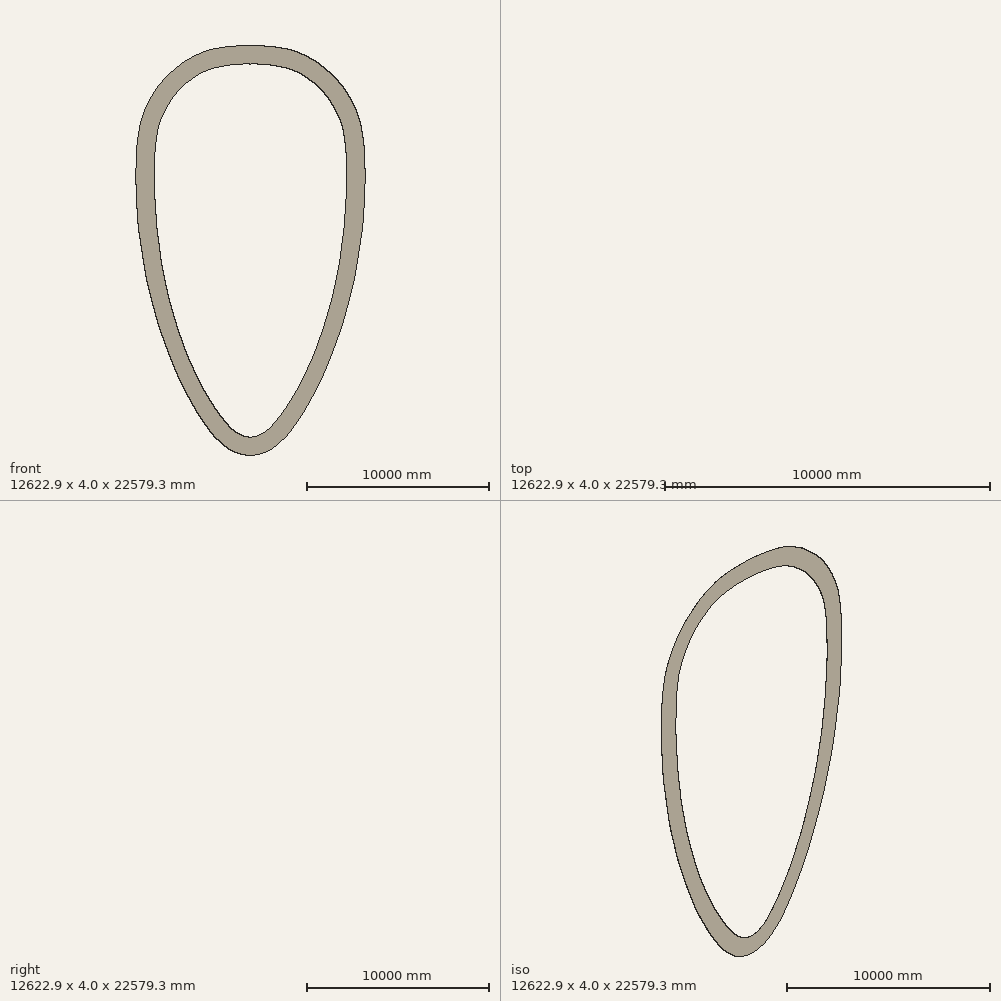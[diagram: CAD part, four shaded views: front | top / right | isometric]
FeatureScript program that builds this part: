
annotation { "Feature Type Name" : "Feature", "Feature Type Description" : "" }
export const myFeature = defineFeature(function(context is Context, id is Id, definition is map)
    precondition{}
    {
        {
            var Q0;
            Q0=qCreatedBy(makeId("Front.planeOp"),FACE);
            var sketch = newSketch(context, id + "F0", { "sketchPlane" : qUnion([Q0])});
            skLineSegment(sketch, "E0", {"start": v(0, -11289.64) * mm, "end": v(-7.01, -11162.82) * mm});
            skLineSegment(sketch, "E1", {"start": v(-7.01, -11162.82) * mm, "end": v(0, -11289.64) * mm});
            skLineSegment(sketch, "E2", {"start": v(0, -11289.64) * mm, "end": v(-111.94, -11283.44) * mm});
            skLineSegment(sketch, "E3", {"start": v(-111.94, -11283.44) * mm, "end": v(-223.42, -11271.8) * mm});
            skLineSegment(sketch, "E4", {"start": v(-223.42, -11271.8) * mm, "end": v(-504.04, -11216.64) * mm});
            skLineSegment(sketch, "E5", {"start": v(-504.04, -11216.64) * mm, "end": v(-777.95, -11130.79) * mm});
            skLineSegment(sketch, "E6", {"start": v(-777.95, -11130.79) * mm, "end": v(-980.67, -11048.11) * mm});
            skLineSegment(sketch, "E7", {"start": v(-980.67, -11048.11) * mm, "end": v(-1172.64, -10945.8) * mm});
            skLineSegment(sketch, "E8", {"start": v(-1172.64, -10945.8) * mm, "end": v(-1407.5, -10773.28) * mm});
            skLineSegment(sketch, "E9", {"start": v(-1407.5, -10773.28) * mm, "end": v(-1628.17, -10579.5) * mm});
            skLineSegment(sketch, "E10", {"start": v(-1628.17, -10579.5) * mm, "end": v(-1825.42, -10402.14) * mm});
            skLineSegment(sketch, "E11", {"start": v(-1825.42, -10402.14) * mm, "end": v(-2012.87, -10216.57) * mm});
            skLineSegment(sketch, "E12", {"start": v(-2012.87, -10216.57) * mm, "end": v(-2227.38, -9954.46) * mm});
            skLineSegment(sketch, "E13", {"start": v(-2227.38, -9954.46) * mm, "end": v(-2424.63, -9676.9) * mm});
            skLineSegment(sketch, "E14", {"start": v(-2424.63, -9676.9) * mm, "end": v(-2700.9, -9278.24) * mm});
            skLineSegment(sketch, "E15", {"start": v(-2700.9, -9278.24) * mm, "end": v(-2963.4, -8872.04) * mm});
            skLineSegment(sketch, "E16", {"start": v(-2963.4, -8872.04) * mm, "end": v(-3166.72, -8516.54) * mm});
            skLineSegment(sketch, "E17", {"start": v(-3166.72, -8516.54) * mm, "end": v(-3362.58, -8156.37) * mm});
            skLineSegment(sketch, "E18", {"start": v(-3362.58, -8156.37) * mm, "end": v(-3412.39, -8065.52) * mm});
            skLineSegment(sketch, "E19", {"start": v(-3412.39, -8065.52) * mm, "end": v(-3575.86, -7775.73) * mm});
            skLineSegment(sketch, "E20", {"start": v(-3575.86, -7775.73) * mm, "end": v(-3757.6, -7429.63) * mm});
            skLineSegment(sketch, "E21", {"start": v(-3757.6, -7429.63) * mm, "end": v(-3926.43, -7077.15) * mm});
            skLineSegment(sketch, "E22", {"start": v(-3926.43, -7077.15) * mm, "end": v(-4036.82, -6824.98) * mm});
            skLineSegment(sketch, "E23", {"start": v(-4036.82, -6824.98) * mm, "end": v(-4141.67, -6570.42) * mm});
            skLineSegment(sketch, "E24", {"start": v(-4141.67, -6570.42) * mm, "end": v(-4331.8, -6091.94) * mm});
            skLineSegment(sketch, "E25", {"start": v(-4331.8, -6091.94) * mm, "end": v(-4436, -5835.24) * mm});
            skLineSegment(sketch, "E26", {"start": v(-4436, -5835.24) * mm, "end": v(-4538.65, -5577.94) * mm});
            skLineSegment(sketch, "E27", {"start": v(-4538.65, -5577.94) * mm, "end": v(-4659.73, -5254.02) * mm});
            skLineSegment(sketch, "E28", {"start": v(-4659.73, -5254.02) * mm, "end": v(-4776.7, -4928.49) * mm});
            skLineSegment(sketch, "E29", {"start": v(-4776.7, -4928.49) * mm, "end": v(-4898.87, -4588.51) * mm});
            skLineSegment(sketch, "E30", {"start": v(-4898.87, -4588.51) * mm, "end": v(-5017.16, -4247.21) * mm});
            skLineSegment(sketch, "E31", {"start": v(-5017.16, -4247.21) * mm, "end": v(-5124.27, -3909.8) * mm});
            skLineSegment(sketch, "E32", {"start": v(-5124.27, -3909.8) * mm, "end": v(-5221.15, -3569.3) * mm});
            skLineSegment(sketch, "E33", {"start": v(-5221.15, -3569.3) * mm, "end": v(-5238.27, -3504.46) * mm});
            skLineSegment(sketch, "E34", {"start": v(-5238.27, -3504.46) * mm, "end": v(-5325.82, -3176.37) * mm});
            skLineSegment(sketch, "E35", {"start": v(-5325.82, -3176.37) * mm, "end": v(-5411.01, -2847.6) * mm});
            skLineSegment(sketch, "E36", {"start": v(-5411.01, -2847.6) * mm, "end": v(-5529.91, -2400.35) * mm});
            skLineSegment(sketch, "E37", {"start": v(-5529.91, -2400.35) * mm, "end": v(-5642.94, -1951.71) * mm});
            skLineSegment(sketch, "E38", {"start": v(-5642.94, -1951.71) * mm, "end": v(-5743.55, -1477.9) * mm});
            skLineSegment(sketch, "E39", {"start": v(-5743.55, -1477.9) * mm, "end": v(-5829.55, -1001.01) * mm});
            skLineSegment(sketch, "E40", {"start": v(-5829.55, -1001.01) * mm, "end": v(-5936.31, -331.14) * mm});
            skLineSegment(sketch, "E41", {"start": v(-5936.31, -331.14) * mm, "end": v(-5988.84, 26.4) * mm});
            skLineSegment(sketch, "E42", {"start": v(-5988.84, 26.4) * mm, "end": v(-6043.32, 383.62) * mm});
            skLineSegment(sketch, "E43", {"start": v(-6043.32, 383.62) * mm, "end": v(-6096.81, 707.31) * mm});
            skLineSegment(sketch, "E44", {"start": v(-6096.81, 707.31) * mm, "end": v(-6146.65, 1031.52) * mm});
            skLineSegment(sketch, "E45", {"start": v(-6146.65, 1031.52) * mm, "end": v(-6183.68, 1335.68) * mm});
            skLineSegment(sketch, "E46", {"start": v(-6183.68, 1335.68) * mm, "end": v(-6057.6, 1351.03) * mm});
            skLineSegment(sketch, "E47", {"start": v(-6057.6, 1351.03) * mm, "end": v(-6183.68, 1335.68) * mm});
            skLineSegment(sketch, "E48", {"start": v(-6183.68, 1335.68) * mm, "end": v(-6226.6, 1881.8) * mm});
            skLineSegment(sketch, "E49", {"start": v(-6226.6, 1881.8) * mm, "end": v(-6258.26, 2428.67) * mm});
            skLineSegment(sketch, "E50", {"start": v(-6258.26, 2428.67) * mm, "end": v(-6272.23, 2791.2) * mm});
            skLineSegment(sketch, "E51", {"start": v(-6272.23, 2791.2) * mm, "end": v(-6285.94, 3153.77) * mm});
            skLineSegment(sketch, "E52", {"start": v(-6285.94, 3153.77) * mm, "end": v(-6300.55, 3466.54) * mm});
            skLineSegment(sketch, "E53", {"start": v(-6300.55, 3466.54) * mm, "end": v(-6311.37, 3779.4) * mm});
            skLineSegment(sketch, "E54", {"start": v(-6311.37, 3779.4) * mm, "end": v(-6311.47, 4250.1) * mm});
            skLineSegment(sketch, "E55", {"start": v(-6311.47, 4250.1) * mm, "end": v(-6310.8, 4321.48) * mm});
            skLineSegment(sketch, "E56", {"start": v(-6310.8, 4321.48) * mm, "end": v(-6183.8, 4320.29) * mm});
            skLineSegment(sketch, "E57", {"start": v(-6183.8, 4320.29) * mm, "end": v(-6310.8, 4321.48) * mm});
            skLineSegment(sketch, "E58", {"start": v(-6310.8, 4321.48) * mm, "end": v(-6297.68, 4798.67) * mm});
            skLineSegment(sketch, "E59", {"start": v(-6297.68, 4798.67) * mm, "end": v(-6272.6, 5435.52) * mm});
            skLineSegment(sketch, "E60", {"start": v(-6272.6, 5435.52) * mm, "end": v(-6258.69, 5683.58) * mm});
            skLineSegment(sketch, "E61", {"start": v(-6258.69, 5683.58) * mm, "end": v(-6237.5, 5930.98) * mm});
            skLineSegment(sketch, "E62", {"start": v(-6237.5, 5930.98) * mm, "end": v(-6203.85, 6188.94) * mm});
            skLineSegment(sketch, "E63", {"start": v(-6203.85, 6188.94) * mm, "end": v(-6162.65, 6445.94) * mm});
            skLineSegment(sketch, "E64", {"start": v(-6162.65, 6445.94) * mm, "end": v(-6110.12, 6747.69) * mm});
            skLineSegment(sketch, "E65", {"start": v(-6110.12, 6747.69) * mm, "end": v(-6051.35, 7048.2) * mm});
            skLineSegment(sketch, "E66", {"start": v(-6051.35, 7048.2) * mm, "end": v(-5926.7, 7023.81) * mm});
            skLineSegment(sketch, "E67", {"start": v(-5926.7, 7023.81) * mm, "end": v(-6051.35, 7048.2) * mm});
            skLineSegment(sketch, "E68", {"start": v(-6051.35, 7048.2) * mm, "end": v(-6042.96, 7077.02) * mm});
            skLineSegment(sketch, "E69", {"start": v(-6042.96, 7077.02) * mm, "end": v(-6029.68, 7122.08) * mm});
            skLineSegment(sketch, "E70", {"start": v(-6029.68, 7122.08) * mm, "end": v(-5926.38, 7441.9) * mm});
            skLineSegment(sketch, "E71", {"start": v(-5926.38, 7441.9) * mm, "end": v(-5868.31, 7599.55) * mm});
            skLineSegment(sketch, "E72", {"start": v(-5868.31, 7599.55) * mm, "end": v(-5805.22, 7755.18) * mm});
            skLineSegment(sketch, "E73", {"start": v(-5805.22, 7755.18) * mm, "end": v(-5655.36, 8075.96) * mm});
            skLineSegment(sketch, "E74", {"start": v(-5655.36, 8075.96) * mm, "end": v(-5489.37, 8389.29) * mm});
            skLineSegment(sketch, "E75", {"start": v(-5489.37, 8389.29) * mm, "end": v(-5349.98, 8633.54) * mm});
            skLineSegment(sketch, "E76", {"start": v(-5349.98, 8633.54) * mm, "end": v(-5197.63, 8869.15) * mm});
            skLineSegment(sketch, "E77", {"start": v(-5197.63, 8869.15) * mm, "end": v(-5044.92, 9070.62) * mm});
            skLineSegment(sketch, "E78", {"start": v(-5044.92, 9070.62) * mm, "end": v(-4884.22, 9266.38) * mm});
            skLineSegment(sketch, "E79", {"start": v(-4884.22, 9266.38) * mm, "end": v(-4774.2, 9397.95) * mm});
            skLineSegment(sketch, "E80", {"start": v(-4774.2, 9397.95) * mm, "end": v(-4659.93, 9525.56) * mm});
            skLineSegment(sketch, "E81", {"start": v(-4659.93, 9525.56) * mm, "end": v(-4549.3, 9635.08) * mm});
            skLineSegment(sketch, "E82", {"start": v(-4549.3, 9635.08) * mm, "end": v(-4432.96, 9738.61) * mm});
            skLineSegment(sketch, "E83", {"start": v(-4432.96, 9738.61) * mm, "end": v(-4348.53, 9643.74) * mm});
            skLineSegment(sketch, "E84", {"start": v(-4348.53, 9643.74) * mm, "end": v(-4432.96, 9738.61) * mm});
            skLineSegment(sketch, "E85", {"start": v(-4432.96, 9738.61) * mm, "end": v(-4092.55, 10032.06) * mm});
            skLineSegment(sketch, "E86", {"start": v(-4092.55, 10032.06) * mm, "end": v(-3818.92, 10253.22) * mm});
            skLineSegment(sketch, "E87", {"start": v(-3818.92, 10253.22) * mm, "end": v(-3693.57, 10351.47) * mm});
            skLineSegment(sketch, "E88", {"start": v(-3693.57, 10351.47) * mm, "end": v(-3563.44, 10442.37) * mm});
            skLineSegment(sketch, "E89", {"start": v(-3563.44, 10442.37) * mm, "end": v(-3397.07, 10536.07) * mm});
            skLineSegment(sketch, "E90", {"start": v(-3397.07, 10536.07) * mm, "end": v(-3226.64, 10623.58) * mm});
            skLineSegment(sketch, "E91", {"start": v(-3226.64, 10623.58) * mm, "end": v(-3085.77, 10700.23) * mm});
            skLineSegment(sketch, "E92", {"start": v(-3085.77, 10700.23) * mm, "end": v(-2943.68, 10773.84) * mm});
            skLineSegment(sketch, "E93", {"start": v(-2943.68, 10773.84) * mm, "end": v(-2811.25, 10832.34) * mm});
            skLineSegment(sketch, "E94", {"start": v(-2811.25, 10832.34) * mm, "end": v(-2677.62, 10888.8) * mm});
            skLineSegment(sketch, "E95", {"start": v(-2677.62, 10888.8) * mm, "end": v(-2562.5, 10940.26) * mm});
            skLineSegment(sketch, "E96", {"start": v(-2562.5, 10940.26) * mm, "end": v(-2446.17, 10987.91) * mm});
            skLineSegment(sketch, "E97", {"start": v(-2446.17, 10987.91) * mm, "end": v(-2293.52, 11034.06) * mm});
            skLineSegment(sketch, "E98", {"start": v(-2293.52, 11034.06) * mm, "end": v(-2137.44, 11070.06) * mm});
            skLineSegment(sketch, "E99", {"start": v(-2137.44, 11070.06) * mm, "end": v(-1844.04, 11131.85) * mm});
            skLineSegment(sketch, "E100", {"start": v(-1844.04, 11131.85) * mm, "end": v(-1549.48, 11183.54) * mm});
            skLineSegment(sketch, "E101", {"start": v(-1549.48, 11183.54) * mm, "end": v(-1246.78, 11220.3) * mm});
            skLineSegment(sketch, "E102", {"start": v(-1246.78, 11220.3) * mm, "end": v(-942.8, 11248.44) * mm});
            skLineSegment(sketch, "E103", {"start": v(-942.8, 11248.44) * mm, "end": v(-598.45, 11277) * mm});
            skLineSegment(sketch, "E104", {"start": v(-598.45, 11277) * mm, "end": v(-299.39, 11289.51) * mm});
            skLineSegment(sketch, "E105", {"start": v(-299.39, 11289.51) * mm, "end": v(0, 11289.64) * mm});
            skLineSegment(sketch, "E106", {"start": v(0, 11289.64) * mm, "end": v(0.05, 11162.64) * mm});
            skLineSegment(sketch, "E107", {"start": v(0.05, 11162.64) * mm, "end": v(0, 11289.64) * mm});
            skLineSegment(sketch, "E108", {"start": v(0, 11289.64) * mm, "end": v(299.36, 11289.51) * mm});
            skLineSegment(sketch, "E109", {"start": v(299.36, 11289.51) * mm, "end": v(598.42, 11277) * mm});
            skLineSegment(sketch, "E110", {"start": v(598.42, 11277) * mm, "end": v(942.8, 11248.44) * mm});
            skLineSegment(sketch, "E111", {"start": v(942.8, 11248.44) * mm, "end": v(1246.78, 11220.3) * mm});
            skLineSegment(sketch, "E112", {"start": v(1246.78, 11220.3) * mm, "end": v(1549.48, 11183.54) * mm});
            skLineSegment(sketch, "E113", {"start": v(1549.48, 11183.54) * mm, "end": v(1844.04, 11131.85) * mm});
            skLineSegment(sketch, "E114", {"start": v(1844.04, 11131.85) * mm, "end": v(2137.44, 11070.06) * mm});
            skLineSegment(sketch, "E115", {"start": v(2137.44, 11070.06) * mm, "end": v(2293.5, 11034.06) * mm});
            skLineSegment(sketch, "E116", {"start": v(2293.5, 11034.06) * mm, "end": v(2446.15, 10987.91) * mm});
            skLineSegment(sketch, "E117", {"start": v(2446.15, 10987.91) * mm, "end": v(2562.5, 10940.26) * mm});
            skLineSegment(sketch, "E118", {"start": v(2562.5, 10940.26) * mm, "end": v(2677.6, 10888.8) * mm});
            skLineSegment(sketch, "E119", {"start": v(2677.6, 10888.8) * mm, "end": v(2811.25, 10832.34) * mm});
            skLineSegment(sketch, "E120", {"start": v(2811.25, 10832.34) * mm, "end": v(2943.68, 10773.84) * mm});
            skLineSegment(sketch, "E121", {"start": v(2943.68, 10773.84) * mm, "end": v(3085.74, 10700.23) * mm});
            skLineSegment(sketch, "E122", {"start": v(3085.74, 10700.23) * mm, "end": v(3226.61, 10623.58) * mm});
            skLineSegment(sketch, "E123", {"start": v(3226.61, 10623.58) * mm, "end": v(3397.07, 10536.07) * mm});
            skLineSegment(sketch, "E124", {"start": v(3397.07, 10536.07) * mm, "end": v(3563.44, 10442.37) * mm});
            skLineSegment(sketch, "E125", {"start": v(3563.44, 10442.37) * mm, "end": v(3693.57, 10351.47) * mm});
            skLineSegment(sketch, "E126", {"start": v(3693.57, 10351.47) * mm, "end": v(3818.9, 10253.22) * mm});
            skLineSegment(sketch, "E127", {"start": v(3818.9, 10253.22) * mm, "end": v(4092.55, 10032.06) * mm});
            skLineSegment(sketch, "E128", {"start": v(4092.55, 10032.06) * mm, "end": v(4432.96, 9738.61) * mm});
            skLineSegment(sketch, "E129", {"start": v(4432.96, 9738.61) * mm, "end": v(4350.03, 9642.42) * mm});
            skLineSegment(sketch, "E130", {"start": v(4350.03, 9642.42) * mm, "end": v(4432.96, 9738.61) * mm});
            skLineSegment(sketch, "E131", {"start": v(4432.96, 9738.61) * mm, "end": v(4549.3, 9635.08) * mm});
            skLineSegment(sketch, "E132", {"start": v(4549.3, 9635.08) * mm, "end": v(4659.93, 9525.56) * mm});
            skLineSegment(sketch, "E133", {"start": v(4659.93, 9525.56) * mm, "end": v(4774.2, 9397.95) * mm});
            skLineSegment(sketch, "E134", {"start": v(4774.2, 9397.95) * mm, "end": v(4884.22, 9266.38) * mm});
            skLineSegment(sketch, "E135", {"start": v(4884.22, 9266.38) * mm, "end": v(5044.92, 9070.62) * mm});
            skLineSegment(sketch, "E136", {"start": v(5044.92, 9070.62) * mm, "end": v(5197.6, 8869.15) * mm});
            skLineSegment(sketch, "E137", {"start": v(5197.6, 8869.15) * mm, "end": v(5349.95, 8633.54) * mm});
            skLineSegment(sketch, "E138", {"start": v(5349.95, 8633.54) * mm, "end": v(5489.35, 8389.29) * mm});
            skLineSegment(sketch, "E139", {"start": v(5489.35, 8389.29) * mm, "end": v(5655.36, 8075.96) * mm});
            skLineSegment(sketch, "E140", {"start": v(5655.36, 8075.96) * mm, "end": v(5805.2, 7755.18) * mm});
            skLineSegment(sketch, "E141", {"start": v(5805.2, 7755.18) * mm, "end": v(5868.31, 7599.55) * mm});
            skLineSegment(sketch, "E142", {"start": v(5868.31, 7599.55) * mm, "end": v(5926.38, 7441.9) * mm});
            skLineSegment(sketch, "E143", {"start": v(5926.38, 7441.9) * mm, "end": v(6029.68, 7122.08) * mm});
            skLineSegment(sketch, "E144", {"start": v(6029.68, 7122.08) * mm, "end": v(6042.96, 7077.02) * mm});
            skLineSegment(sketch, "E145", {"start": v(6042.96, 7077.02) * mm, "end": v(6051.32, 7048.2) * mm});
            skLineSegment(sketch, "E146", {"start": v(6051.32, 7048.2) * mm, "end": v(5929.38, 7012.79) * mm});
            skLineSegment(sketch, "E147", {"start": v(5929.38, 7012.79) * mm, "end": v(6051.32, 7048.2) * mm});
            skLineSegment(sketch, "E148", {"start": v(6051.32, 7048.2) * mm, "end": v(6110.12, 6747.69) * mm});
            skLineSegment(sketch, "E149", {"start": v(6110.12, 6747.69) * mm, "end": v(6162.62, 6445.94) * mm});
            skLineSegment(sketch, "E150", {"start": v(6162.62, 6445.94) * mm, "end": v(6203.85, 6188.94) * mm});
            skLineSegment(sketch, "E151", {"start": v(6203.85, 6188.94) * mm, "end": v(6237.48, 5930.98) * mm});
            skLineSegment(sketch, "E152", {"start": v(6237.48, 5930.98) * mm, "end": v(6258.69, 5683.58) * mm});
            skLineSegment(sketch, "E153", {"start": v(6258.69, 5683.58) * mm, "end": v(6272.6, 5435.52) * mm});
            skLineSegment(sketch, "E154", {"start": v(6272.6, 5435.52) * mm, "end": v(6297.68, 4798.67) * mm});
            skLineSegment(sketch, "E155", {"start": v(6297.68, 4798.67) * mm, "end": v(6310.78, 4321.48) * mm});
            skLineSegment(sketch, "E156", {"start": v(6310.78, 4321.48) * mm, "end": v(6183.83, 4317.97) * mm});
            skLineSegment(sketch, "E157", {"start": v(6183.83, 4317.97) * mm, "end": v(6310.78, 4321.48) * mm});
            skLineSegment(sketch, "E158", {"start": v(6310.78, 4321.48) * mm, "end": v(6311.47, 4250.1) * mm});
            skLineSegment(sketch, "E159", {"start": v(6311.47, 4250.1) * mm, "end": v(6311.37, 3779.4) * mm});
            skLineSegment(sketch, "E160", {"start": v(6311.37, 3779.4) * mm, "end": v(6300.52, 3466.54) * mm});
            skLineSegment(sketch, "E161", {"start": v(6300.52, 3466.54) * mm, "end": v(6285.94, 3153.77) * mm});
            skLineSegment(sketch, "E162", {"start": v(6285.94, 3153.77) * mm, "end": v(6272.2, 2791.2) * mm});
            skLineSegment(sketch, "E163", {"start": v(6272.2, 2791.2) * mm, "end": v(6258.26, 2428.67) * mm});
            skLineSegment(sketch, "E164", {"start": v(6258.26, 2428.67) * mm, "end": v(6226.58, 1881.8) * mm});
            skLineSegment(sketch, "E165", {"start": v(6226.58, 1881.8) * mm, "end": v(6183.68, 1335.68) * mm});
            skLineSegment(sketch, "E166", {"start": v(6183.68, 1335.68) * mm, "end": v(6057.06, 1345.64) * mm});
            skLineSegment(sketch, "E167", {"start": v(6057.06, 1345.64) * mm, "end": v(6183.68, 1335.68) * mm});
            skLineSegment(sketch, "E168", {"start": v(6183.68, 1335.68) * mm, "end": v(6146.65, 1031.52) * mm});
            skLineSegment(sketch, "E169", {"start": v(6146.65, 1031.52) * mm, "end": v(6096.79, 707.31) * mm});
            skLineSegment(sketch, "E170", {"start": v(6096.79, 707.31) * mm, "end": v(6043.32, 383.62) * mm});
            skLineSegment(sketch, "E171", {"start": v(6043.32, 383.62) * mm, "end": v(5988.81, 26.4) * mm});
            skLineSegment(sketch, "E172", {"start": v(5988.81, 26.4) * mm, "end": v(5936.31, -331.14) * mm});
            skLineSegment(sketch, "E173", {"start": v(5936.31, -331.14) * mm, "end": v(5829.55, -1001.01) * mm});
            skLineSegment(sketch, "E174", {"start": v(5829.55, -1001.01) * mm, "end": v(5743.55, -1477.9) * mm});
            skLineSegment(sketch, "E175", {"start": v(5743.55, -1477.9) * mm, "end": v(5642.94, -1951.71) * mm});
            skLineSegment(sketch, "E176", {"start": v(5642.94, -1951.71) * mm, "end": v(5529.91, -2400.35) * mm});
            skLineSegment(sketch, "E177", {"start": v(5529.91, -2400.35) * mm, "end": v(5410.99, -2847.6) * mm});
            skLineSegment(sketch, "E178", {"start": v(5410.99, -2847.6) * mm, "end": v(5325.82, -3176.37) * mm});
            skLineSegment(sketch, "E179", {"start": v(5325.82, -3176.37) * mm, "end": v(5238.27, -3504.46) * mm});
            skLineSegment(sketch, "E180", {"start": v(5238.27, -3504.46) * mm, "end": v(5221.12, -3569.3) * mm});
            skLineSegment(sketch, "E181", {"start": v(5221.12, -3569.3) * mm, "end": v(5124.27, -3909.8) * mm});
            skLineSegment(sketch, "E182", {"start": v(5124.27, -3909.8) * mm, "end": v(5017.14, -4247.21) * mm});
            skLineSegment(sketch, "E183", {"start": v(5017.14, -4247.21) * mm, "end": v(4898.87, -4588.51) * mm});
            skLineSegment(sketch, "E184", {"start": v(4898.87, -4588.51) * mm, "end": v(4776.7, -4928.49) * mm});
            skLineSegment(sketch, "E185", {"start": v(4776.7, -4928.49) * mm, "end": v(4659.73, -5254.02) * mm});
            skLineSegment(sketch, "E186", {"start": v(4659.73, -5254.02) * mm, "end": v(4538.65, -5577.94) * mm});
            skLineSegment(sketch, "E187", {"start": v(4538.65, -5577.94) * mm, "end": v(4435.98, -5835.24) * mm});
            skLineSegment(sketch, "E188", {"start": v(4435.98, -5835.24) * mm, "end": v(4331.8, -6091.94) * mm});
            skLineSegment(sketch, "E189", {"start": v(4331.8, -6091.94) * mm, "end": v(4141.67, -6570.42) * mm});
            skLineSegment(sketch, "E190", {"start": v(4141.67, -6570.42) * mm, "end": v(4036.82, -6824.98) * mm});
            skLineSegment(sketch, "E191", {"start": v(4036.82, -6824.98) * mm, "end": v(3926.43, -7077.15) * mm});
            skLineSegment(sketch, "E192", {"start": v(3926.43, -7077.15) * mm, "end": v(3757.57, -7429.63) * mm});
            skLineSegment(sketch, "E193", {"start": v(3757.57, -7429.63) * mm, "end": v(3575.86, -7775.73) * mm});
            skLineSegment(sketch, "E194", {"start": v(3575.86, -7775.73) * mm, "end": v(3412.39, -8065.52) * mm});
            skLineSegment(sketch, "E195", {"start": v(3412.39, -8065.52) * mm, "end": v(3362.58, -8156.37) * mm});
            skLineSegment(sketch, "E196", {"start": v(3362.58, -8156.37) * mm, "end": v(3166.72, -8516.54) * mm});
            skLineSegment(sketch, "E197", {"start": v(3166.72, -8516.54) * mm, "end": v(2963.37, -8872.04) * mm});
            skLineSegment(sketch, "E198", {"start": v(2963.37, -8872.04) * mm, "end": v(2700.9, -9278.24) * mm});
            skLineSegment(sketch, "E199", {"start": v(2700.9, -9278.24) * mm, "end": v(2424.63, -9676.9) * mm});
            skLineSegment(sketch, "E200", {"start": v(2424.63, -9676.9) * mm, "end": v(2227.38, -9954.46) * mm});
            skLineSegment(sketch, "E201", {"start": v(2227.38, -9954.46) * mm, "end": v(2012.87, -10216.57) * mm});
            skLineSegment(sketch, "E202", {"start": v(2012.87, -10216.57) * mm, "end": v(1825.42, -10402.14) * mm});
            skLineSegment(sketch, "E203", {"start": v(1825.42, -10402.14) * mm, "end": v(1628.17, -10579.5) * mm});
            skLineSegment(sketch, "E204", {"start": v(1628.17, -10579.5) * mm, "end": v(1407.5, -10773.28) * mm});
            skLineSegment(sketch, "E205", {"start": v(1407.5, -10773.28) * mm, "end": v(1172.64, -10945.8) * mm});
            skLineSegment(sketch, "E206", {"start": v(1172.64, -10945.8) * mm, "end": v(980.64, -11048.11) * mm});
            skLineSegment(sketch, "E207", {"start": v(980.64, -11048.11) * mm, "end": v(777.95, -11130.79) * mm});
            skLineSegment(sketch, "E208", {"start": v(777.95, -11130.79) * mm, "end": v(504.01, -11216.64) * mm});
            skLineSegment(sketch, "E209", {"start": v(504.01, -11216.64) * mm, "end": v(223.42, -11271.8) * mm});
            skLineSegment(sketch, "E210", {"start": v(223.42, -11271.8) * mm, "end": v(111.94, -11283.44) * mm});
            skLineSegment(sketch, "E211", {"start": v(111.94, -11283.44) * mm, "end": v(0, -11289.64) * mm});
            skLineSegment(sketch, "E212", {"start": v(0, 10265.23) * mm, "end": v(0, 10392.23) * mm});
            skLineSegment(sketch, "E213", {"start": v(0, 10392.23) * mm, "end": v(0, 10265.23) * mm});
            skLineSegment(sketch, "E214", {"start": v(0, 10265.23) * mm, "end": v(-81.61, 10275.32) * mm});
            skLineSegment(sketch, "E215", {"start": v(-81.61, 10275.32) * mm, "end": v(-163.65, 10280.1) * mm});
            skLineSegment(sketch, "E216", {"start": v(-163.65, 10280.1) * mm, "end": v(-273.76, 10277.25) * mm});
            skLineSegment(sketch, "E217", {"start": v(-273.76, 10277.25) * mm, "end": v(-383.84, 10269.32) * mm});
            skLineSegment(sketch, "E218", {"start": v(-383.84, 10269.32) * mm, "end": v(-668.8, 10252.76) * mm});
            skLineSegment(sketch, "E219", {"start": v(-668.8, 10252.76) * mm, "end": v(-953.1, 10232.64) * mm});
            skLineSegment(sketch, "E220", {"start": v(-953.1, 10232.64) * mm, "end": v(-1208.6, 10199.7) * mm});
            skLineSegment(sketch, "E221", {"start": v(-1208.6, 10199.7) * mm, "end": v(-1462.74, 10156.16) * mm});
            skLineSegment(sketch, "E222", {"start": v(-1462.74, 10156.16) * mm, "end": v(-1503.83, 10148.57) * mm});
            skLineSegment(sketch, "E223", {"start": v(-1503.83, 10148.57) * mm, "end": v(-1823.14, 10083.44) * mm});
            skLineSegment(sketch, "E224", {"start": v(-1823.14, 10083.44) * mm, "end": v(-1981.28, 10044.56) * mm});
            skLineSegment(sketch, "E225", {"start": v(-1981.28, 10044.56) * mm, "end": v(-2137.8, 9999.47) * mm});
            skLineSegment(sketch, "E226", {"start": v(-2137.8, 9999.47) * mm, "end": v(-2433.57, 9891.57) * mm});
            skLineSegment(sketch, "E227", {"start": v(-2433.57, 9891.57) * mm, "end": v(-2718.38, 9756.88) * mm});
            skLineSegment(sketch, "E228", {"start": v(-2718.38, 9756.88) * mm, "end": v(-2920.14, 9640.87) * mm});
            skLineSegment(sketch, "E229", {"start": v(-2920.14, 9640.87) * mm, "end": v(-3112.92, 9510.95) * mm});
            skLineSegment(sketch, "E230", {"start": v(-3112.92, 9510.95) * mm, "end": v(-3230.27, 9422.54) * mm});
            skLineSegment(sketch, "E231", {"start": v(-3230.27, 9422.54) * mm, "end": v(-3347.64, 9334.12) * mm});
            skLineSegment(sketch, "E232", {"start": v(-3347.64, 9334.12) * mm, "end": v(-3461.64, 9253.04) * mm});
            skLineSegment(sketch, "E233", {"start": v(-3461.64, 9253.04) * mm, "end": v(-3573.65, 9169.48) * mm});
            skLineSegment(sketch, "E234", {"start": v(-3573.65, 9169.48) * mm, "end": v(-3657.2, 9098.05) * mm});
            skLineSegment(sketch, "E235", {"start": v(-3657.2, 9098.05) * mm, "end": v(-3736.95, 9022.38) * mm});
            skLineSegment(sketch, "E236", {"start": v(-3736.95, 9022.38) * mm, "end": v(-3824.38, 9114.51) * mm});
            skLineSegment(sketch, "E237", {"start": v(-3824.38, 9114.51) * mm, "end": v(-3736.95, 9022.38) * mm});
            skLineSegment(sketch, "E238", {"start": v(-3736.95, 9022.38) * mm, "end": v(-3755.09, 9004.15) * mm});
            skLineSegment(sketch, "E239", {"start": v(-3755.09, 9004.15) * mm, "end": v(-3927, 8819.7) * mm});
            skLineSegment(sketch, "E240", {"start": v(-3927, 8819.7) * mm, "end": v(-4065.65, 8663.46) * mm});
            skLineSegment(sketch, "E241", {"start": v(-4065.65, 8663.46) * mm, "end": v(-4197.4, 8501.71) * mm});
            skLineSegment(sketch, "E242", {"start": v(-4197.4, 8501.71) * mm, "end": v(-4317.54, 8331.76) * mm});
            skLineSegment(sketch, "E243", {"start": v(-4317.54, 8331.76) * mm, "end": v(-4429.96, 8156.24) * mm});
            skLineSegment(sketch, "E244", {"start": v(-4429.96, 8156.24) * mm, "end": v(-4546.3, 7966.46) * mm});
            skLineSegment(sketch, "E245", {"start": v(-4546.3, 7966.46) * mm, "end": v(-4657.37, 7773.62) * mm});
            skLineSegment(sketch, "E246", {"start": v(-4657.37, 7773.62) * mm, "end": v(-4809.9, 7473.67) * mm});
            skLineSegment(sketch, "E247", {"start": v(-4809.9, 7473.67) * mm, "end": v(-4940.22, 7163.51) * mm});
            skLineSegment(sketch, "E248", {"start": v(-4940.22, 7163.51) * mm, "end": v(-5007.48, 6970.88) * mm});
            skLineSegment(sketch, "E249", {"start": v(-5007.48, 6970.88) * mm, "end": v(-5067.3, 6775.83) * mm});
            skLineSegment(sketch, "E250", {"start": v(-5067.3, 6775.83) * mm, "end": v(-5188.71, 6813.07) * mm});
            skLineSegment(sketch, "E251", {"start": v(-5188.71, 6813.07) * mm, "end": v(-5067.3, 6775.83) * mm});
            skLineSegment(sketch, "E252", {"start": v(-5067.3, 6775.83) * mm, "end": v(-5108.04, 6565.93) * mm});
            skLineSegment(sketch, "E253", {"start": v(-5108.04, 6565.93) * mm, "end": v(-5157.34, 6277.64) * mm});
            skLineSegment(sketch, "E254", {"start": v(-5157.34, 6277.64) * mm, "end": v(-5199.48, 5988.15) * mm});
            skLineSegment(sketch, "E255", {"start": v(-5199.48, 5988.15) * mm, "end": v(-5237.58, 5664.1) * mm});
            skLineSegment(sketch, "E256", {"start": v(-5237.58, 5664.1) * mm, "end": v(-5263.1, 5339) * mm});
            skLineSegment(sketch, "E257", {"start": v(-5263.1, 5339) * mm, "end": v(-5274.7, 5003.52) * mm});
            skLineSegment(sketch, "E258", {"start": v(-5274.7, 5003.52) * mm, "end": v(-5280.15, 4667.73) * mm});
            skLineSegment(sketch, "E259", {"start": v(-5280.15, 4667.73) * mm, "end": v(-5289.07, 4274) * mm});
            skLineSegment(sketch, "E260", {"start": v(-5289.07, 4274) * mm, "end": v(-5416.02, 4276.88) * mm});
            skLineSegment(sketch, "E261", {"start": v(-5416.02, 4276.88) * mm, "end": v(-5289.07, 4274) * mm});
            skLineSegment(sketch, "E262", {"start": v(-5289.07, 4274) * mm, "end": v(-5289.9, 4156.35) * mm});
            skLineSegment(sketch, "E263", {"start": v(-5289.9, 4156.35) * mm, "end": v(-5293.23, 3618.5) * mm});
            skLineSegment(sketch, "E264", {"start": v(-5293.23, 3618.5) * mm, "end": v(-5281.55, 3179.2) * mm});
            skLineSegment(sketch, "E265", {"start": v(-5281.55, 3179.2) * mm, "end": v(-5243.37, 2537.66) * mm});
            skLineSegment(sketch, "E266", {"start": v(-5243.37, 2537.66) * mm, "end": v(-5205.2, 1985.52) * mm});
            skLineSegment(sketch, "E267", {"start": v(-5205.2, 1985.52) * mm, "end": v(-5161.81, 1335.68) * mm});
            skLineSegment(sketch, "E268", {"start": v(-5161.81, 1335.68) * mm, "end": v(-5288.53, 1327.23) * mm});
            skLineSegment(sketch, "E269", {"start": v(-5288.53, 1327.23) * mm, "end": v(-5161.81, 1335.68) * mm});
            skLineSegment(sketch, "E270", {"start": v(-5161.81, 1335.68) * mm, "end": v(-5102.23, 820.06) * mm});
            skLineSegment(sketch, "E271", {"start": v(-5102.23, 820.06) * mm, "end": v(-5044.7, 421.92) * mm});
            skLineSegment(sketch, "E272", {"start": v(-5044.7, 421.92) * mm, "end": v(-4990.5, -25.32) * mm});
            skLineSegment(sketch, "E273", {"start": v(-4990.5, -25.32) * mm, "end": v(-4933.7, -472.03) * mm});
            skLineSegment(sketch, "E274", {"start": v(-4933.7, -472.03) * mm, "end": v(-4842.84, -984.6) * mm});
            skLineSegment(sketch, "E275", {"start": v(-4842.84, -984.6) * mm, "end": v(-4737.56, -1495.04) * mm});
            skLineSegment(sketch, "E276", {"start": v(-4737.56, -1495.04) * mm, "end": v(-4623.18, -2053) * mm});
            skLineSegment(sketch, "E277", {"start": v(-4623.18, -2053) * mm, "end": v(-4496.59, -2607.72) * mm});
            skLineSegment(sketch, "E278", {"start": v(-4496.59, -2607.72) * mm, "end": v(-4390.64, -2998.06) * mm});
            skLineSegment(sketch, "E279", {"start": v(-4390.64, -2998.06) * mm, "end": v(-4277.77, -3386.73) * mm});
            skLineSegment(sketch, "E280", {"start": v(-4277.77, -3386.73) * mm, "end": v(-4153.59, -3813.94) * mm});
            skLineSegment(sketch, "E281", {"start": v(-4153.59, -3813.94) * mm, "end": v(-4023.49, -4239.16) * mm});
            skLineSegment(sketch, "E282", {"start": v(-4023.49, -4239.16) * mm, "end": v(-3917.85, -4555.95) * mm});
            skLineSegment(sketch, "E283", {"start": v(-3917.85, -4555.95) * mm, "end": v(-3809, -4871.85) * mm});
            skLineSegment(sketch, "E284", {"start": v(-3809, -4871.85) * mm, "end": v(-3660.93, -5299.94) * mm});
            skLineSegment(sketch, "E285", {"start": v(-3660.93, -5299.94) * mm, "end": v(-3500.48, -5723) * mm});
            skLineSegment(sketch, "E286", {"start": v(-3500.48, -5723) * mm, "end": v(-3334.97, -6099.2) * mm});
            skLineSegment(sketch, "E287", {"start": v(-3334.97, -6099.2) * mm, "end": v(-3161.8, -6472.5) * mm});
            skLineSegment(sketch, "E288", {"start": v(-3161.8, -6472.5) * mm, "end": v(-2942, -6956.68) * mm});
            skLineSegment(sketch, "E289", {"start": v(-2942, -6956.68) * mm, "end": v(-2706.3, -7432.4) * mm});
            skLineSegment(sketch, "E290", {"start": v(-2706.3, -7432.4) * mm, "end": v(-2500.88, -7789.42) * mm});
            skLineSegment(sketch, "E291", {"start": v(-2500.88, -7789.42) * mm, "end": v(-2325.42, -8087.08) * mm});
            skLineSegment(sketch, "E292", {"start": v(-2325.42, -8087.08) * mm, "end": v(-2146.35, -8382.56) * mm});
            skLineSegment(sketch, "E293", {"start": v(-2146.35, -8382.56) * mm, "end": v(-1956.1, -8677.35) * mm});
            skLineSegment(sketch, "E294", {"start": v(-1956.1, -8677.35) * mm, "end": v(-1755.37, -8964.83) * mm});
            skLineSegment(sketch, "E295", {"start": v(-1755.37, -8964.83) * mm, "end": v(-1523.6, -9268.28) * mm});
            skLineSegment(sketch, "E296", {"start": v(-1523.6, -9268.28) * mm, "end": v(-1278.59, -9562.47) * mm});
            skLineSegment(sketch, "E297", {"start": v(-1278.59, -9562.47) * mm, "end": v(-1096.82, -9761.75) * mm});
            skLineSegment(sketch, "E298", {"start": v(-1096.82, -9761.75) * mm, "end": v(-897.15, -9940.95) * mm});
            skLineSegment(sketch, "E299", {"start": v(-897.15, -9940.95) * mm, "end": v(-679.58, -10082.43) * mm});
            skLineSegment(sketch, "E300", {"start": v(-679.58, -10082.43) * mm, "end": v(-443.33, -10192.51) * mm});
            skLineSegment(sketch, "E301", {"start": v(-443.33, -10192.51) * mm, "end": v(-343.2, -10228.38) * mm});
            skLineSegment(sketch, "E302", {"start": v(-343.2, -10228.38) * mm, "end": v(-240.7, -10255.5) * mm});
            skLineSegment(sketch, "E303", {"start": v(-240.7, -10255.5) * mm, "end": v(-120.93, -10271.91) * mm});
            skLineSegment(sketch, "E304", {"start": v(-120.93, -10271.91) * mm, "end": v(0, -10273.61) * mm});
            skLineSegment(sketch, "E305", {"start": v(0, -10273.61) * mm, "end": v(-1.8, -10400.61) * mm});
            skLineSegment(sketch, "E306", {"start": v(-1.8, -10400.61) * mm, "end": v(0, -10273.61) * mm});
            skLineSegment(sketch, "E307", {"start": v(0, -10273.61) * mm, "end": v(120.93, -10271.91) * mm});
            skLineSegment(sketch, "E308", {"start": v(120.93, -10271.91) * mm, "end": v(240.7, -10255.5) * mm});
            skLineSegment(sketch, "E309", {"start": v(240.7, -10255.5) * mm, "end": v(343.18, -10228.38) * mm});
            skLineSegment(sketch, "E310", {"start": v(343.18, -10228.38) * mm, "end": v(443.33, -10192.51) * mm});
            skLineSegment(sketch, "E311", {"start": v(443.33, -10192.51) * mm, "end": v(679.55, -10082.43) * mm});
            skLineSegment(sketch, "E312", {"start": v(679.55, -10082.43) * mm, "end": v(897.15, -9940.95) * mm});
            skLineSegment(sketch, "E313", {"start": v(897.15, -9940.95) * mm, "end": v(1096.82, -9761.75) * mm});
            skLineSegment(sketch, "E314", {"start": v(1096.82, -9761.75) * mm, "end": v(1278.59, -9562.47) * mm});
            skLineSegment(sketch, "E315", {"start": v(1278.59, -9562.47) * mm, "end": v(1523.57, -9268.28) * mm});
            skLineSegment(sketch, "E316", {"start": v(1523.57, -9268.28) * mm, "end": v(1755.37, -8964.83) * mm});
            skLineSegment(sketch, "E317", {"start": v(1755.37, -8964.83) * mm, "end": v(1956.1, -8677.35) * mm});
            skLineSegment(sketch, "E318", {"start": v(1956.1, -8677.35) * mm, "end": v(2146.35, -8382.56) * mm});
            skLineSegment(sketch, "E319", {"start": v(2146.35, -8382.56) * mm, "end": v(2325.42, -8087.08) * mm});
            skLineSegment(sketch, "E320", {"start": v(2325.42, -8087.08) * mm, "end": v(2500.88, -7789.42) * mm});
            skLineSegment(sketch, "E321", {"start": v(2500.88, -7789.42) * mm, "end": v(2706.3, -7432.4) * mm});
            skLineSegment(sketch, "E322", {"start": v(2706.3, -7432.4) * mm, "end": v(2942, -6956.68) * mm});
            skLineSegment(sketch, "E323", {"start": v(2942, -6956.68) * mm, "end": v(3161.8, -6472.5) * mm});
            skLineSegment(sketch, "E324", {"start": v(3161.8, -6472.5) * mm, "end": v(3334.97, -6099.2) * mm});
            skLineSegment(sketch, "E325", {"start": v(3334.97, -6099.2) * mm, "end": v(3500.48, -5723) * mm});
            skLineSegment(sketch, "E326", {"start": v(3500.48, -5723) * mm, "end": v(3660.93, -5299.94) * mm});
            skLineSegment(sketch, "E327", {"start": v(3660.93, -5299.94) * mm, "end": v(3808.98, -4871.85) * mm});
            skLineSegment(sketch, "E328", {"start": v(3808.98, -4871.85) * mm, "end": v(3917.85, -4555.95) * mm});
            skLineSegment(sketch, "E329", {"start": v(3917.85, -4555.95) * mm, "end": v(4023.49, -4239.16) * mm});
            skLineSegment(sketch, "E330", {"start": v(4023.49, -4239.16) * mm, "end": v(4153.59, -3813.94) * mm});
            skLineSegment(sketch, "E331", {"start": v(4153.59, -3813.94) * mm, "end": v(4277.77, -3386.73) * mm});
            skLineSegment(sketch, "E332", {"start": v(4277.77, -3386.73) * mm, "end": v(4390.64, -2998.06) * mm});
            skLineSegment(sketch, "E333", {"start": v(4390.64, -2998.06) * mm, "end": v(4496.56, -2607.72) * mm});
            skLineSegment(sketch, "E334", {"start": v(4496.56, -2607.72) * mm, "end": v(4623.18, -2053) * mm});
            skLineSegment(sketch, "E335", {"start": v(4623.18, -2053) * mm, "end": v(4737.53, -1495.04) * mm});
            skLineSegment(sketch, "E336", {"start": v(4737.53, -1495.04) * mm, "end": v(4842.81, -984.6) * mm});
            skLineSegment(sketch, "E337", {"start": v(4842.81, -984.6) * mm, "end": v(4933.7, -472.03) * mm});
            skLineSegment(sketch, "E338", {"start": v(4933.7, -472.03) * mm, "end": v(4990.47, -25.32) * mm});
            skLineSegment(sketch, "E339", {"start": v(4990.47, -25.32) * mm, "end": v(5044.7, 421.92) * mm});
            skLineSegment(sketch, "E340", {"start": v(5044.7, 421.92) * mm, "end": v(5102.23, 820.06) * mm});
            skLineSegment(sketch, "E341", {"start": v(5102.23, 820.06) * mm, "end": v(5161.81, 1335.68) * mm});
            skLineSegment(sketch, "E342", {"start": v(5161.81, 1335.68) * mm, "end": v(5287.98, 1321.1) * mm});
            skLineSegment(sketch, "E343", {"start": v(5287.98, 1321.1) * mm, "end": v(5161.81, 1335.68) * mm});
            skLineSegment(sketch, "E344", {"start": v(5161.81, 1335.68) * mm, "end": v(5205.2, 1985.52) * mm});
            skLineSegment(sketch, "E345", {"start": v(5205.2, 1985.52) * mm, "end": v(5243.37, 2537.66) * mm});
            skLineSegment(sketch, "E346", {"start": v(5243.37, 2537.66) * mm, "end": v(5281.55, 3179.2) * mm});
            skLineSegment(sketch, "E347", {"start": v(5281.55, 3179.2) * mm, "end": v(5293.23, 3618.5) * mm});
            skLineSegment(sketch, "E348", {"start": v(5293.23, 3618.5) * mm, "end": v(5289.9, 4156.35) * mm});
            skLineSegment(sketch, "E349", {"start": v(5289.9, 4156.35) * mm, "end": v(5289.04, 4274) * mm});
            skLineSegment(sketch, "E350", {"start": v(5289.04, 4274) * mm, "end": v(5416.04, 4274.92) * mm});
            skLineSegment(sketch, "E351", {"start": v(5416.04, 4274.92) * mm, "end": v(5289.04, 4274) * mm});
            skLineSegment(sketch, "E352", {"start": v(5289.04, 4274) * mm, "end": v(5280.15, 4667.73) * mm});
            skLineSegment(sketch, "E353", {"start": v(5280.15, 4667.73) * mm, "end": v(5274.7, 5003.52) * mm});
            skLineSegment(sketch, "E354", {"start": v(5274.7, 5003.52) * mm, "end": v(5263.1, 5339) * mm});
            skLineSegment(sketch, "E355", {"start": v(5263.1, 5339) * mm, "end": v(5237.56, 5664.1) * mm});
            skLineSegment(sketch, "E356", {"start": v(5237.56, 5664.1) * mm, "end": v(5199.46, 5988.15) * mm});
            skLineSegment(sketch, "E357", {"start": v(5199.46, 5988.15) * mm, "end": v(5157.34, 6277.64) * mm});
            skLineSegment(sketch, "E358", {"start": v(5157.34, 6277.64) * mm, "end": v(5108.04, 6565.93) * mm});
            skLineSegment(sketch, "E359", {"start": v(5108.04, 6565.93) * mm, "end": v(5067.3, 6775.83) * mm});
            skLineSegment(sketch, "E360", {"start": v(5067.3, 6775.83) * mm, "end": v(5191.96, 6800.01) * mm});
            skLineSegment(sketch, "E361", {"start": v(5191.96, 6800.01) * mm, "end": v(5067.3, 6775.83) * mm});
            skLineSegment(sketch, "E362", {"start": v(5067.3, 6775.83) * mm, "end": v(5007.48, 6970.88) * mm});
            skLineSegment(sketch, "E363", {"start": v(5007.48, 6970.88) * mm, "end": v(4940.22, 7163.51) * mm});
            skLineSegment(sketch, "E364", {"start": v(4940.22, 7163.51) * mm, "end": v(4809.87, 7473.67) * mm});
            skLineSegment(sketch, "E365", {"start": v(4809.87, 7473.67) * mm, "end": v(4657.37, 7773.62) * mm});
            skLineSegment(sketch, "E366", {"start": v(4657.37, 7773.62) * mm, "end": v(4546.3, 7966.46) * mm});
            skLineSegment(sketch, "E367", {"start": v(4546.3, 7966.46) * mm, "end": v(4429.96, 8156.24) * mm});
            skLineSegment(sketch, "E368", {"start": v(4429.96, 8156.24) * mm, "end": v(4317.54, 8331.76) * mm});
            skLineSegment(sketch, "E369", {"start": v(4317.54, 8331.76) * mm, "end": v(4197.4, 8501.71) * mm});
            skLineSegment(sketch, "E370", {"start": v(4197.4, 8501.71) * mm, "end": v(4065.65, 8663.46) * mm});
            skLineSegment(sketch, "E371", {"start": v(4065.65, 8663.46) * mm, "end": v(3927, 8819.7) * mm});
            skLineSegment(sketch, "E372", {"start": v(3927, 8819.7) * mm, "end": v(3755.09, 9004.15) * mm});
            skLineSegment(sketch, "E373", {"start": v(3755.09, 9004.15) * mm, "end": v(3736.95, 9022.38) * mm});
            skLineSegment(sketch, "E374", {"start": v(3736.95, 9022.38) * mm, "end": v(3826.97, 9111.97) * mm});
            skLineSegment(sketch, "E375", {"start": v(3826.97, 9111.97) * mm, "end": v(3736.95, 9022.38) * mm});
            skLineSegment(sketch, "E376", {"start": v(3736.95, 9022.38) * mm, "end": v(3657.2, 9098.05) * mm});
            skLineSegment(sketch, "E377", {"start": v(3657.2, 9098.05) * mm, "end": v(3573.65, 9169.48) * mm});
            skLineSegment(sketch, "E378", {"start": v(3573.65, 9169.48) * mm, "end": v(3461.61, 9253.04) * mm});
            skLineSegment(sketch, "E379", {"start": v(3461.61, 9253.04) * mm, "end": v(3347.62, 9334.12) * mm});
            skLineSegment(sketch, "E380", {"start": v(3347.62, 9334.12) * mm, "end": v(3230.27, 9422.54) * mm});
            skLineSegment(sketch, "E381", {"start": v(3230.27, 9422.54) * mm, "end": v(3112.92, 9510.95) * mm});
            skLineSegment(sketch, "E382", {"start": v(3112.92, 9510.95) * mm, "end": v(2920.11, 9640.87) * mm});
            skLineSegment(sketch, "E383", {"start": v(2920.11, 9640.87) * mm, "end": v(2718.36, 9756.88) * mm});
            skLineSegment(sketch, "E384", {"start": v(2718.36, 9756.88) * mm, "end": v(2433.57, 9891.57) * mm});
            skLineSegment(sketch, "E385", {"start": v(2433.57, 9891.57) * mm, "end": v(2137.8, 9999.47) * mm});
            skLineSegment(sketch, "E386", {"start": v(2137.8, 9999.47) * mm, "end": v(1981.28, 10044.56) * mm});
            skLineSegment(sketch, "E387", {"start": v(1981.28, 10044.56) * mm, "end": v(1823.11, 10083.44) * mm});
            skLineSegment(sketch, "E388", {"start": v(1823.11, 10083.44) * mm, "end": v(1503.83, 10148.57) * mm});
            skLineSegment(sketch, "E389", {"start": v(1503.83, 10148.57) * mm, "end": v(1462.74, 10156.16) * mm});
            skLineSegment(sketch, "E390", {"start": v(1462.74, 10156.16) * mm, "end": v(1208.6, 10199.7) * mm});
            skLineSegment(sketch, "E391", {"start": v(1208.6, 10199.7) * mm, "end": v(953.1, 10232.64) * mm});
            skLineSegment(sketch, "E392", {"start": v(953.1, 10232.64) * mm, "end": v(668.8, 10252.76) * mm});
            skLineSegment(sketch, "E393", {"start": v(668.8, 10252.76) * mm, "end": v(383.84, 10269.32) * mm});
            skLineSegment(sketch, "E394", {"start": v(383.84, 10269.32) * mm, "end": v(273.74, 10277.25) * mm});
            skLineSegment(sketch, "E395", {"start": v(273.74, 10277.25) * mm, "end": v(163.63, 10280.1) * mm});
            skLineSegment(sketch, "E396", {"start": v(163.63, 10280.1) * mm, "end": v(81.61, 10275.32) * mm});
            skLineSegment(sketch, "E397", {"start": v(81.61, 10275.32) * mm, "end": v(0, 10265.23) * mm});
            skSolve(sketch);
        }
        {
            var Q0;
            Q0 = qSketchRegion(id + "F0", true);
            extrude(context, id + "F1", {"entities" : qUnion([Q0]), "depth" : 4 * mm, "offsetDistance" : 25 * mm});
        }
    });
